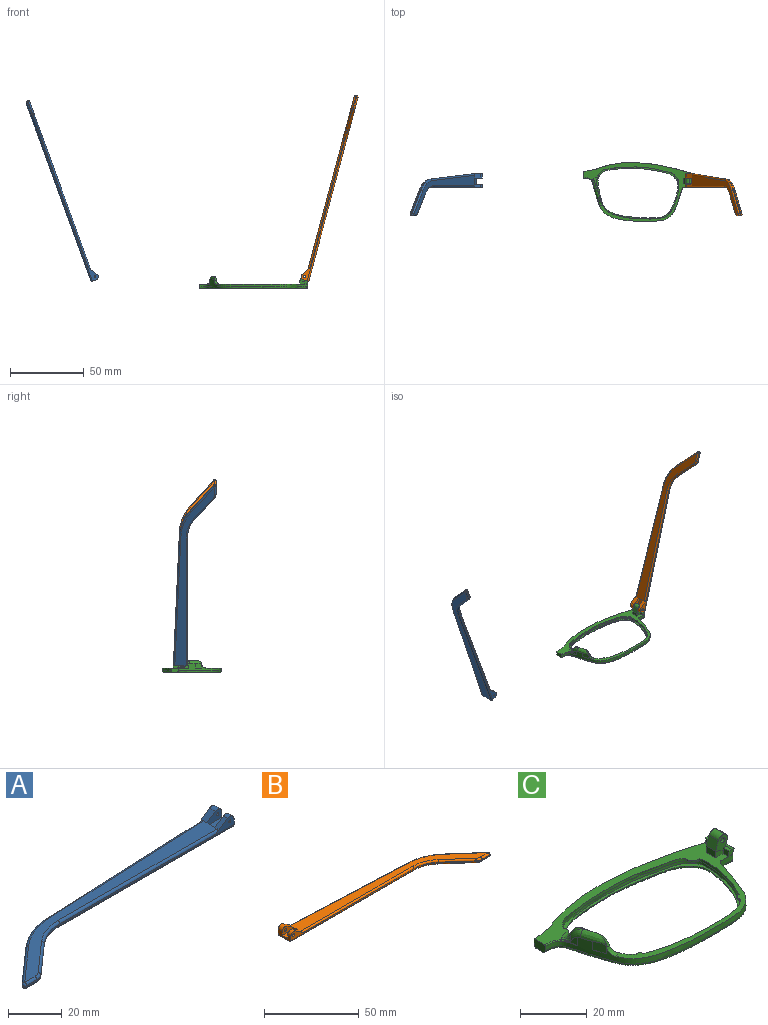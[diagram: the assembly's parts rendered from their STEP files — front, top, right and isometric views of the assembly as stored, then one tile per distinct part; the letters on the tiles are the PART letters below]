
ASSEMBLY  parts=3 mates=1
PART A: 43 faces, bbox 130.2x29.5x5.9 mm
  f0: plane 9.62x3.72mm, normal (1,0,0), area 24.7mm2, adj f1,f3,f4,f5,f10,f16,f18,f28
  f1: cylinder r=2.2mm len=3.45mm, axis (0,-1,0), area 11mm2, adj f0,f2,f4,f37
  f2: plane 6.01x3.91mm, normal (-0.55,0,0.84), area 12.7mm2, adj f1,f4,f9,f19,f37
  f3: plane 2.26x0.1mm, normal (0,0,1), area 0.1mm2, adj f0,f5,f18
  f4: plane 92.1x4.9mm, normal (0,-1,0), area 79.9mm2, adj f0,f1,f2,f14,f19,f36,f42
  f5: plane 93.42x4.13mm, normal (-0.04,1,0), area 64.8mm2, adj f0,f3,f11,f15,f17,f27,f28
  f6: plane 17.82x15.72mm, normal (-0.66,0.75,0), area 14.3mm2, adj f11,f12,f25,f30
  f7: plane 5.46x0.6mm, normal (0,-1,0), area 3.3mm2, adj f12,f13,f23,f32
  f8: plane 14.99x13.23mm, normal (0.66,-0.75,0), area 12mm2, adj f13,f14,f21,f34
  f9: plane 121.18x26.73mm, normal (0,0,1), area 627.7mm2, adj f2,f17,f19,f20,f21,f22,f23,f25
  f10: plane 129.1x27.08mm, normal (0,0,-1), area 686.5mm2, adj f0,f28,f29,f30,f32,f33,f34,f35
  f11: cylinder r=30mm len=18.52mm, axis (0,0,-1), area 12.2mm2, adj f5,f6,f26,f29
  f12: cylinder r=1mm len=1.75mm, axis (0,0,-1), area 1.5mm2, adj f6,f7,f24,f31
  f13: cylinder r=5mm len=3.31mm, axis (0,0,-1), area 2.2mm2, adj f7,f8,f22,f33
  f14: cylinder r=20mm len=13.23mm, axis (0,0,1), area 8.7mm2, adj f4,f8,f20,f35
  f15: plane 5.66x0.25mm, normal (0,0,-1), area 0.7mm2, adj f5,f17,f18
  f16: cylinder r=2.2mm len=3.45mm, axis (0,-1,0), area 14.8mm2, adj f0,f17,f18,f38
  f17: plane 6.01x3.91mm, normal (-0.55,0,0.84), area 16.9mm2, adj f5,f9,f15,f16,f18,f27,f38
  f18: plane 7.92x3.3mm, normal (0,1,0), area 15.9mm2, adj f0,f3,f15,f16,f17,f41
  f19: cylinder r=1mm len=84.18mm, axis (-1,0,0), area 131.4mm2, adj f2,f4,f9,f20
  f20: torus R=21mm, axis (0,0,1), area 23.1mm2, adj f9,f14,f19,f21
  f21: cylinder r=1mm len=15.65mm, axis (-0.75,-0.66,0), area 31.4mm2, adj f8,f9,f20,f22
  f22: torus R=4mm, axis (0,0,1), area 5.3mm2, adj f9,f13,f21,f23
  f23: cylinder r=1mm len=5.46mm, axis (-1,0,0), area 8.6mm2, adj f7,f9,f22,f24
  f24: sphere r=1mm, area 2.4mm2, adj f12,f23,f25
  f25: cylinder r=1mm len=18.48mm, axis (0.75,0.66,0), area 37.3mm2, adj f6,f9,f24,f26
  f26: torus R=29mm, axis (0,0,1), area 31.6mm2, adj f9,f11,f25,f27
  f27: cylinder r=1mm len=85.5mm, axis (1,0.04,0), area 133.5mm2, adj f5,f9,f17,f26
  f28: cylinder r=1mm len=93.46mm, axis (-1,-0.04,0), area 146.9mm2, adj f0,f5,f10,f29
  f29: torus R=29mm, axis (0,0,1), area 31.6mm2, adj f10,f11,f28,f30
  f30: cylinder r=1mm len=18.48mm, axis (-0.75,-0.66,0), area 37.3mm2, adj f6,f10,f29,f31
  f31: sphere r=1mm, area 2.4mm2, adj f12,f30,f32
  f32: cylinder r=1mm len=5.46mm, axis (1,0,0), area 8.6mm2, adj f7,f10,f31,f33
  f33: torus R=4mm, axis (0,0,1), area 5.3mm2, adj f10,f13,f32,f34
  f34: cylinder r=1mm len=15.65mm, axis (0.75,0.66,0), area 31.4mm2, adj f8,f10,f33,f35
  f35: torus R=21mm, axis (0,0,1), area 23.1mm2, adj f10,f14,f34,f36
  f36: cylinder r=1mm len=92.1mm, axis (1,0,0), area 144.7mm2, adj f0,f4,f10,f35
  f37: plane 7.92x4.7mm, normal (0,1,0), area 27mm2, adj f0,f1,f2,f39,f40,f42
  f38: plane 7.92x4.7mm, normal (0,-1,0), area 27mm2, adj f0,f16,f17,f39,f40,f41
  f39: plane 7.92x4.1mm, normal (0,0,1), area 32.5mm2, adj f0,f37,f38,f40
  f40: plane 4.1x1.4mm, normal (1,0,0), area 5.7mm2, adj f9,f37,f38,f39
  f41: cylinder r=0.5mm len=3.1mm, axis (0,-1,0), area 9.7mm2, adj f18,f38
  f42: cylinder r=0.5mm len=2.3mm, axis (0,-1,0), area 7.2mm2, adj f4,f37
PART B: 43 faces, bbox 130.2x29.5x5.9 mm
  f0: plane 9.62x3.72mm, normal (-1,0,0), area 24.7mm2, adj f1,f3,f4,f5,f10,f16,f18,f28
  f1: cylinder r=2.2mm len=3.45mm, axis (0,-1,0), area 11mm2, adj f0,f2,f4,f37
  f2: plane 6.01x3.91mm, normal (0.55,0,0.84), area 12.7mm2, adj f1,f4,f9,f19,f37
  f3: plane 2.26x0.1mm, normal (0,0,1), area 0.1mm2, adj f0,f5,f18
  f4: plane 92.1x4.9mm, normal (0,-1,0), area 78.2mm2, adj f0,f1,f2,f14,f19,f36,f42
  f5: plane 93.42x4.13mm, normal (0.04,1,0), area 64.8mm2, adj f0,f3,f11,f15,f17,f27,f28
  f6: plane 17.82x15.72mm, normal (0.66,0.75,0), area 14.3mm2, adj f11,f12,f25,f30
  f7: plane 5.46x0.6mm, normal (0,-1,0), area 3.3mm2, adj f12,f13,f23,f32
  f8: plane 14.99x13.23mm, normal (-0.66,-0.75,0), area 12mm2, adj f13,f14,f21,f34
  f9: plane 121.18x26.73mm, normal (0,0,1), area 627.7mm2, adj f2,f17,f19,f20,f21,f22,f23,f25
  f10: plane 129.1x27.08mm, normal (0,0,-1), area 686.5mm2, adj f0,f28,f29,f30,f32,f33,f34,f35
  f11: cylinder r=30mm len=18.52mm, axis (0,0,-1), area 12.2mm2, adj f5,f6,f26,f29
  f12: cylinder r=1mm len=1.75mm, axis (0,0,-1), area 1.5mm2, adj f6,f7,f24,f31
  f13: cylinder r=5mm len=3.31mm, axis (0,0,-1), area 2.2mm2, adj f7,f8,f22,f33
  f14: cylinder r=20mm len=13.23mm, axis (0,0,1), area 8.7mm2, adj f4,f8,f20,f35
  f15: plane 5.66x0.25mm, normal (0,0,-1), area 0.7mm2, adj f5,f17,f18
  f16: cylinder r=2.2mm len=3.45mm, axis (0,-1,0), area 14.8mm2, adj f0,f17,f18,f38
  f17: plane 6.01x3.91mm, normal (0.55,0,0.84), area 16.9mm2, adj f5,f9,f15,f16,f18,f27,f38
  f18: plane 7.92x3.3mm, normal (0,1,0), area 14.3mm2, adj f0,f3,f15,f16,f17,f41
  f19: cylinder r=1mm len=84.18mm, axis (1,0,0), area 131.4mm2, adj f2,f4,f9,f20
  f20: torus R=21mm, axis (0,0,1), area 23.1mm2, adj f9,f14,f19,f21
  f21: cylinder r=1mm len=15.65mm, axis (0.75,-0.66,0), area 31.4mm2, adj f8,f9,f20,f22
  f22: torus R=4mm, axis (0,0,1), area 5.3mm2, adj f9,f13,f21,f23
  f23: cylinder r=1mm len=5.46mm, axis (1,0,0), area 8.6mm2, adj f7,f9,f22,f24
  f24: sphere r=1mm, area 2.4mm2, adj f12,f23,f25
  f25: cylinder r=1mm len=18.48mm, axis (-0.75,0.66,0), area 37.3mm2, adj f6,f9,f24,f26
  f26: torus R=29mm, axis (0,0,1), area 31.6mm2, adj f9,f11,f25,f27
  f27: cylinder r=1mm len=85.5mm, axis (-1,0.04,0), area 133.5mm2, adj f5,f9,f17,f26
  f28: cylinder r=1mm len=93.46mm, axis (1,-0.04,0), area 146.9mm2, adj f0,f5,f10,f29
  f29: torus R=29mm, axis (0,0,1), area 31.6mm2, adj f10,f11,f28,f30
  f30: cylinder r=1mm len=18.48mm, axis (0.75,-0.66,0), area 37.3mm2, adj f6,f10,f29,f31
  f31: sphere r=1mm, area 2.4mm2, adj f12,f30,f32
  f32: cylinder r=1mm len=5.46mm, axis (-1,0,0), area 8.6mm2, adj f7,f10,f31,f33
  f33: torus R=4mm, axis (0,0,1), area 5.3mm2, adj f10,f13,f32,f34
  f34: cylinder r=1mm len=15.65mm, axis (-0.75,0.66,0), area 31.4mm2, adj f8,f10,f33,f35
  f35: torus R=21mm, axis (0,0,1), area 23.1mm2, adj f10,f14,f34,f36
  f36: cylinder r=1mm len=92.1mm, axis (-1,0,0), area 144.7mm2, adj f0,f4,f10,f35
  f37: plane 7.92x4.7mm, normal (0,1,0), area 25.4mm2, adj f0,f1,f2,f39,f40,f42
  f38: plane 7.92x4.7mm, normal (0,-1,0), area 25.4mm2, adj f0,f16,f17,f39,f40,f41
  f39: plane 7.92x4.1mm, normal (0,0,1), area 32.5mm2, adj f0,f37,f38,f40
  f40: plane 4.1x1.4mm, normal (-1,0,0), area 5.7mm2, adj f9,f37,f38,f39
  f41: cylinder r=0.88mm len=3.1mm, axis (0,-1,0), area 17mm2, adj f18,f38
  f42: cylinder r=0.88mm len=2.3mm, axis (0,-1,0), area 12.6mm2, adj f4,f37
PART C: 61 faces, bbox 75.1x40.9x17.9 mm
  f0: bspline ~1.82x1.22mm, area 0.7mm2, adj f2,f7,f38,f53
  f1: plane 74.08x40.46mm, normal (0,0,1), area 427.2mm2, adj f4,f5,f6,f7,f8,f9,f13,f21
  f2: bspline ~6.1x4.93mm, area 12.7mm2, adj f0,f7,f38,f42,f44,f53,f54
  f3: plane 4.46x1.45mm, normal (0,0,1), area 0.1mm2, adj f7,f39
  f4: plane 1.23x0.04mm, normal (0,0,1), area 0mm2, adj f1,f7,f23
  f5: plane 6.97x5.07mm, normal (0,1,0), area 22.7mm2, adj f1,f21,f22,f26,f28,f29,f31,f32
  f6: plane 3.2x2.36mm, normal (0,-1,0), area 5.7mm2, adj f1,f21,f27,f30
  f7: extruded ~73.26x39.84mm, area 292.7mm2, adj f0,f1,f2,f3,f4,f8,f9,f14
  f8: extruded ~35.39x5.69mm, area 72.2mm2, adj f1,f7,f9,f19
  f9: plane 4.83x3.04mm, normal (-1,0,0), area 13.9mm2, adj f1,f7,f8,f10,f14,f19,f58
  f10: plane 72.4x37.85mm, normal (0,0,-1), area 291.2mm2, adj f9,f14,f16,f18,f19,f20
  f11: plane 56.06x35.45mm, normal (0,0,1), area 127mm2, adj f12,f20
  f12: extruded ~55.69x35.36mm, area 160.5mm2, adj f11,f13
  f13: extruded ~55.69x35.36mm, area 226.3mm2, adj f1,f12,f40,f41,f42,f43,f44,f45
  f14: bspline ~73.27x30.39mm, area 161.7mm2, adj f7,f9,f10,f15
  f15: bspline ~1x1mm, area 0.8mm2, adj f7,f14,f16
  f16: bspline ~8.99x1.23mm, area 12.6mm2, adj f7,f10,f15,f17
  f17: bspline ~1.04x1mm, area 0.7mm2, adj f7,f16,f18
  f18: bspline ~45.86x8.59mm, area 59.8mm2, adj f7,f10,f17,f19
  f19: bspline ~37.01x6.7mm, area 56.6mm2, adj f8,f9,f10,f18
  f20: bspline ~56.23x35.9mm, area 235.3mm2, adj f10,f11
  f21: plane 4x2.36mm, normal (-1,0,0), area 9.5mm2, adj f1,f5,f6,f22
  f22: plane 4x0.02mm, normal (0.34,0,0.94), area 0.1mm2, adj f5,f21,f29
  f23: plane 2.76x2.53mm, normal (0,-1,0), area 3.9mm2, adj f4,f27,f28,f36,f57
  f24: plane 7.67x1.6mm, normal (0.94,0,-0.34), area 13mm2, adj f1,f36,f37,f57
  f25: plane 2.1x1.69mm, normal (0,1,0), area 2.8mm2, adj f1,f26,f28,f37,f57
  f26: plane 3.3x2.1mm, normal (-1,0,0), area 6.9mm2, adj f1,f5,f25,f28
  f27: plane 2.35x2.1mm, normal (-1,0,0), area 4.9mm2, adj f1,f6,f23,f28,f30
  f28: plane 9.65x1.24mm, normal (0,0,1), area 8.2mm2, adj f5,f23,f25,f26,f27,f30,f31,f57
  f29: plane 4x3.31mm, normal (-0.94,0,0.34), area 14.1mm2, adj f5,f22,f30,f33
  f30: plane 5.77x5.06mm, normal (0,-1,0), area 17mm2, adj f6,f27,f28,f29,f31,f32,f33,f34
  f31: plane 4x2.21mm, normal (0.94,0,-0.34), area 9.4mm2, adj f5,f28,f30,f34
  f32: plane 4x0.01mm, normal (0.34,0,0.94), area 0mm2, adj f5,f30,f33,f34
  f33: cylinder r=1.98mm len=4mm, axis (0,1,0), area 12.4mm2, adj f5,f29,f30,f32
  f34: cylinder r=1.98mm len=4mm, axis (0,-1,0), area 12.4mm2, adj f5,f30,f31,f32
  f35: cylinder r=0.88mm len=4mm, axis (0,-1,0), area 22mm2, adj f5,f30
  f36: cone r=1mm half-angle=20deg, axis (0,0,1), area 2.3mm2, adj f1,f23,f24,f57
  f37: cylinder r=1mm len=2.28mm, axis (-0.34,0,-0.94), area 3mm2, adj f1,f24,f25,f57
  f38: extruded ~3.67x3.11mm, area 5.9mm2, adj f0,f2,f7,f60
  f39: extruded ~4.44x3.32mm, area 15.1mm2, adj f3,f7,f43,f44,f56
  f40: extruded ~4.98x1.37mm, area 6.6mm2, adj f13,f42
  f41: plane 3.63x0.97mm, normal (0,0,1), area 0.3mm2, adj f13,f42,f44
  f42: bspline ~15.5x15.35mm, area 6.4mm2, adj f2,f13,f40,f41,f55
  f43: bspline ~7.26x7.26mm, area 6.3mm2, adj f13,f39,f44,f56
  f44: bspline ~10.29x4.84mm, area 21.4mm2, adj f2,f7,f13,f39,f41,f43
  f45: plane 3.19x1.37mm, normal (0,0,-1), area 2.1mm2, adj f13,f46
  f46: cylinder r=2.28mm len=3.17mm, axis (0,0,1), area 2.1mm2, adj f1,f13,f45,f55
  f47: plane 3.14x2.79mm, normal (0,0,-1), area 3.9mm2, adj f13,f48
  f48: cylinder r=2.28mm len=3.13mm, axis (0,0,1), area 2.5mm2, adj f1,f13,f47
  f49: plane 1.79x1.31mm, normal (0,0,-1), area 0.9mm2, adj f13,f50
  f50: cylinder r=1.3mm len=1.78mm, axis (0,0,1), area 1.3mm2, adj f1,f13,f49
  f51: plane 1.95x1.68mm, normal (0,0,-1), area 1.5mm2, adj f13,f52
  f52: cylinder r=1.3mm len=1.93mm, axis (0,0,1), area 1.5mm2, adj f1,f13,f51
  f53: bspline ~2.66x2.04mm, area 1.9mm2, adj f0,f2,f7,f54,f59
  f54: bspline ~3.55x3.47mm, area 3.7mm2, adj f1,f2,f53,f55,f59
  f55: bspline ~6.16x4.45mm, area 7.9mm2, adj f1,f13,f42,f46,f54
  f56: bspline ~3.7x3.66mm, area 7.8mm2, adj f1,f7,f13,f39,f43
  f57: plane 9.71x1.44mm, normal (0.34,0,0.94), area 13.9mm2, adj f23,f24,f25,f28,f36,f37
  f58: bspline ~6.38x2.14mm, area 2.6mm2, adj f1,f7,f9,f59
  f59: bspline ~2.1x1.46mm, area 0.6mm2, adj f7,f53,f54,f58
  f60: bspline ~5.24x1.75mm, area 0mm2, adj f7,f38
PLACE A rot(axis=(0,1,0),70deg) t=(-84.77,-5.75,56)mm
PLACE B rot(axis=(0,-1,0),75deg) t=(68.2,-5.75,-61.61)mm
PLACE C t=(10.15,-1.13,-5.77)mm
MATE revolute B.f41 <-> C.f34  axis (0,-1,0) through (81.2,2.72,1.21)mm
